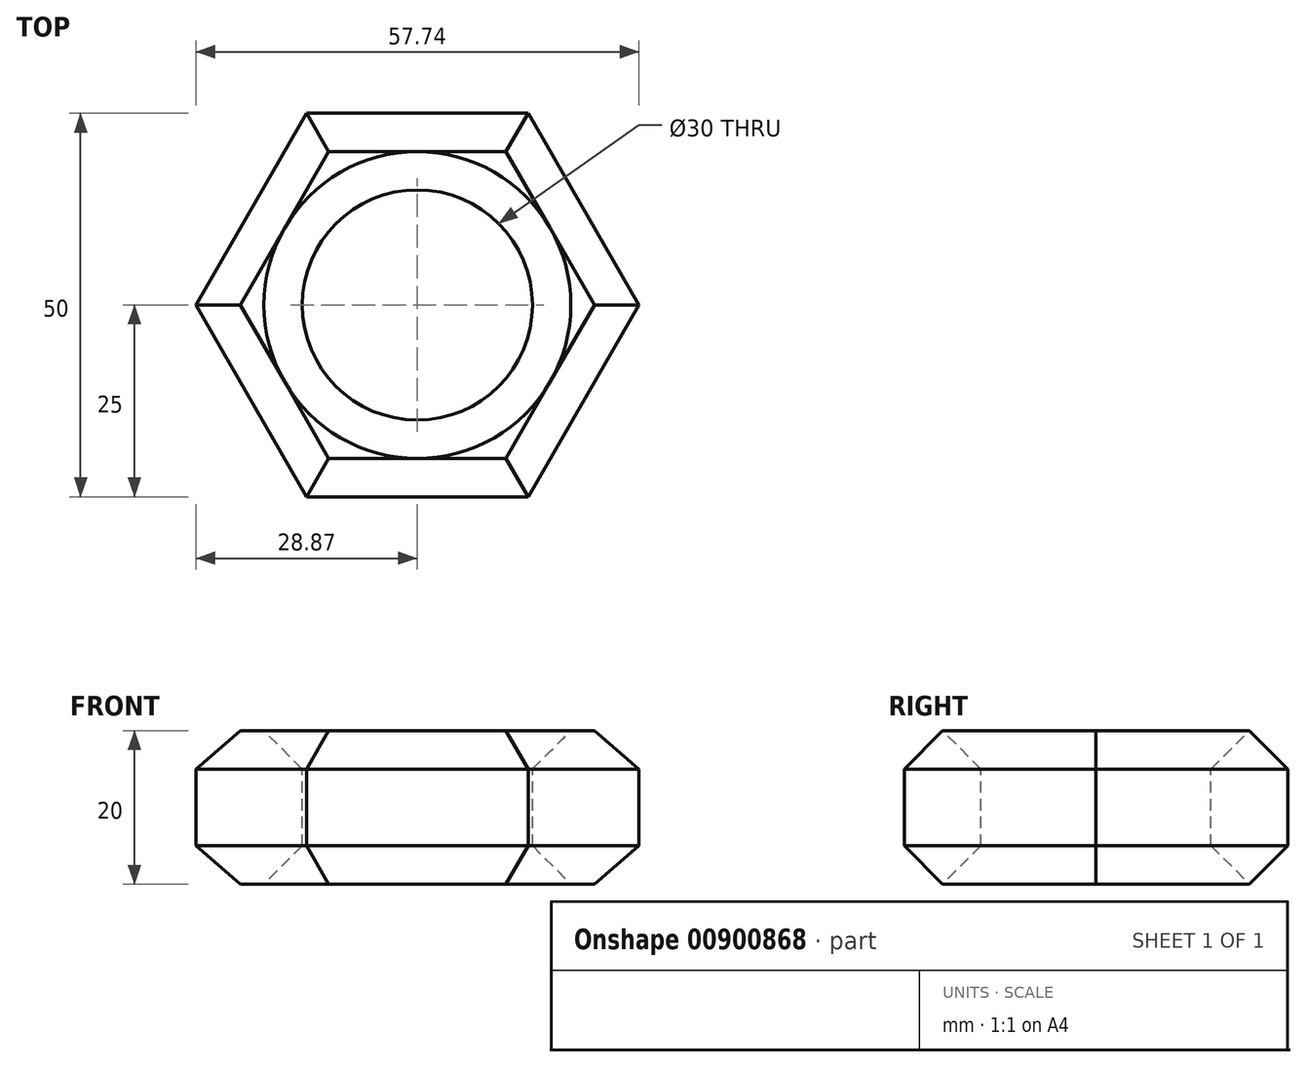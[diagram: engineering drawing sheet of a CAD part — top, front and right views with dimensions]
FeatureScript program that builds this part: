
annotation { "Feature Type Name" : "Feature", "Feature Type Description" : "" }
export const myFeature = defineFeature(function(context is Context, id is Id, definition is map)
    precondition{}
    {
        {
            var Q0;
            Q0=qCreatedBy(makeId("Top.planeOp"),FACE);
            var sketch = newSketch(context, id + "F0", { "sketchPlane" : qUnion([Q0])});
            skCircle(sketch, "E0.cCircle", {"center": v(0, 0) * mm, "radius": 25 * mm, "construction": true});
            skLineSegment(sketch, "E0.0", {"start": v(-14.43, 25) * mm, "end": v(14.43, 25) * mm});
            skLineSegment(sketch, "E0.1", {"start": v(14.43, 25) * mm, "end": v(28.87, 0) * mm});
            skLineSegment(sketch, "E0.2", {"start": v(28.87, 0) * mm, "end": v(14.43, -25) * mm});
            skLineSegment(sketch, "E0.3", {"start": v(14.43, -25) * mm, "end": v(-14.43, -25) * mm});
            skLineSegment(sketch, "E0.4", {"start": v(-14.43, -25) * mm, "end": v(-28.87, 0) * mm});
            skLineSegment(sketch, "E0.5", {"start": v(-28.87, 0) * mm, "end": v(-14.43, 25) * mm});
            skPoint(sketch, "E0.0.midPoint", {"position": v(0, 25) * mm});
            skSolve(sketch);
        }
        {
            var Q0;
            Q0=makeQuery(id+"F0.imprint","IMPRINT",FACE,{"disambiguationData":[TD([[makeQuery(id+"F0.imprint","IMPRINT",EDGE,{"derivedFrom":sQuery(id+"F0.wireOp",EDGE,"E0.0")}),-1.0]])]});
            extrude(context, id + "F1", {"entities" : qUnion([Q0]), "depth" : 20 * mm, "offsetDistance" : 25 * mm});
        }
        {
            var Q0;
            Q0=makeQuery(id+"F1.opExtrude","CAP_FACE",FACE,{"disambiguationData":[OSD([sQuery(id+"F0.wireOp",EDGE,"E0.0"),sQuery(id+"F0.wireOp",EDGE,"E0.1"),sQuery(id+"F0.wireOp",EDGE,"E0.2"),sQuery(id+"F0.wireOp",EDGE,"E0.3"),sQuery(id+"F0.wireOp",EDGE,"E0.4"),sQuery(id+"F0.wireOp",EDGE,"E0.5")])],"isStart":false});
            var sketch = newSketch(context, id + "F2", { "sketchPlane" : qUnion([Q0])});
            skCircle(sketch, "E1", {"center": v(0, 0) * mm, "radius": 15 * mm});
            skSolve(sketch);
        }
        {
            var Q0;
            Q0=makeQuery(id+"F2.imprint","IMPRINT",FACE,{"disambiguationData":[TD([[makeQuery(id+"F2.imprint","IMPRINT",EDGE,{"derivedFrom":sQuery(id+"F2.wireOp",EDGE,"E1")}),1.0]])]});
            extrude(context, id + "F3", {"entities" : qUnion([Q0]), "operationType" : NewBodyOperationType.REMOVE, "oppositeDirection" : true, "depth" : 25 * mm, "offsetDistance" : 25 * mm});
        }
        {
            var Q0;
            Q0=makeQuery(id+"F1.opExtrude","CAP_FACE",FACE,{"disambiguationData":[OSD([sQuery(id+"F0.wireOp",EDGE,"E0.0"),sQuery(id+"F0.wireOp",EDGE,"E0.1"),sQuery(id+"F0.wireOp",EDGE,"E0.2"),sQuery(id+"F0.wireOp",EDGE,"E0.3"),sQuery(id+"F0.wireOp",EDGE,"E0.4"),sQuery(id+"F0.wireOp",EDGE,"E0.5")])],"isStart":false});
            var Q1;
            Q1=makeQuery(id+"F1.opExtrude","CAP_FACE",FACE,{"disambiguationData":[OSD([sQuery(id+"F0.wireOp",EDGE,"E0.0"),sQuery(id+"F0.wireOp",EDGE,"E0.1"),sQuery(id+"F0.wireOp",EDGE,"E0.2"),sQuery(id+"F0.wireOp",EDGE,"E0.3"),sQuery(id+"F0.wireOp",EDGE,"E0.4"),sQuery(id+"F0.wireOp",EDGE,"E0.5")])],"isStart":true});
            chamfer(context, id + "F4", {"entities" : qUnion([Q0, Q1]), "width" : 5 * mm, "tangentPropagation" : true});
        }
    });
